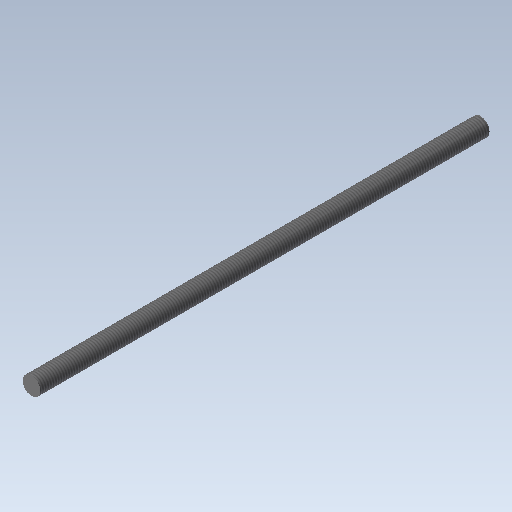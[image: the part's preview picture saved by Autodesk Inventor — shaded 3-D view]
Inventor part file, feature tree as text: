
AUTODESK INVENTOR PART (.ipt)
format: ipt  version: 2021.3 (Build 253353000, 353)  size: 110,592 bytes
history: native  units: mm
features: extrude x1, thread x1, sketch x1
ambient origin geometry x8: Origin, YZ Plane, XZ Plane, XY Plane, X Axis, Y Axis, Z Axis, Center Point
bodies: Solid1 (feature_tree)
feature tree (3):
  extrude  "Extrusion1"  Depth=300.0mm TaperAngle=0.0deg
  thread  "Thread1"  [1 undecoded]
  sketch  "Sketch1"  dims[d0=12.0mm d1=300.0mm d2=0.0mm d3=10.0mm d4=0.0mm]
note: 1 required parameter value undecoded (feature->parameter linkage not recoverable at this tier; creation-order binding heuristic only, values carry confidence <= 0.55)
